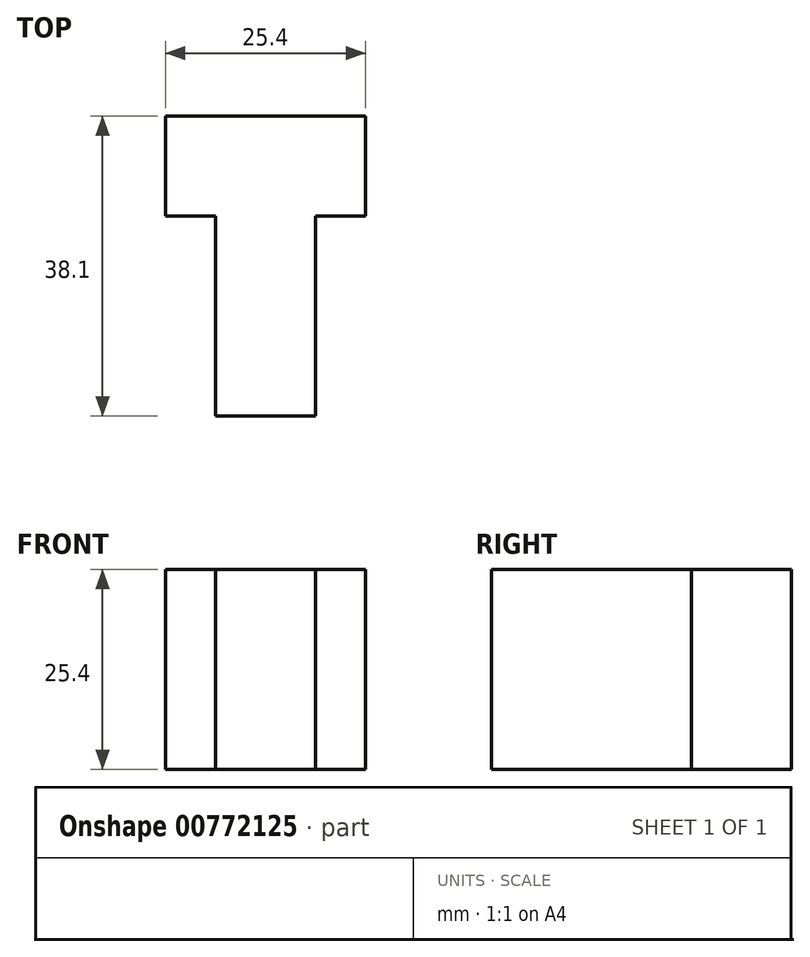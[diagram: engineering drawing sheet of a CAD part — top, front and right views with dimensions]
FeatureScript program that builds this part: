
annotation { "Feature Type Name" : "Feature", "Feature Type Description" : "" }
export const myFeature = defineFeature(function(context is Context, id is Id, definition is map)
    precondition{}
    {
        {
            var Q0;
            Q0=qCreatedBy(makeId("Top.planeOp"),FACE);
            var sketch = newSketch(context, id + "F0", { "sketchPlane" : qUnion([Q0])});
            skLineSegment(sketch, "E0", {"start": v(0, 0) * mm, "end": v(0, 25.4) * mm});
            skLineSegment(sketch, "E1", {"start": v(0, 0) * mm, "end": v(12.7, 0) * mm});
            skLineSegment(sketch, "E2", {"start": v(12.7, 0) * mm, "end": v(12.7, 25.4) * mm});
            skLineSegment(sketch, "E3", {"start": v(12.7, 25.4) * mm, "end": v(19.05, 25.4) * mm});
            skLineSegment(sketch, "E4", {"start": v(19.05, 25.4) * mm, "end": v(19.05, 38.1) * mm});
            skLineSegment(sketch, "E5", {"start": v(19.05, 38.1) * mm, "end": v(-6.35, 38.1) * mm});
            skLineSegment(sketch, "E6", {"start": v(-6.35, 38.1) * mm, "end": v(-6.35, 25.4) * mm});
            skLineSegment(sketch, "E7", {"start": v(-6.35, 25.4) * mm, "end": v(0, 25.4) * mm});
            skSolve(sketch);
        }
        {
            var Q0;
            Q0=makeQuery(id+"F0.imprint","IMPRINT",FACE,{"disambiguationData":[TD([[makeQuery(id+"F0.imprint","IMPRINT",EDGE,{"derivedFrom":sQuery(id+"F0.wireOp",EDGE,"E0")}),-1.0]])]});
            extrude(context, id + "F1", {"entities" : qUnion([Q0]), "depth" : 25.4 * mm, "offsetDistance" : 25.4 * mm});
        }
    });
